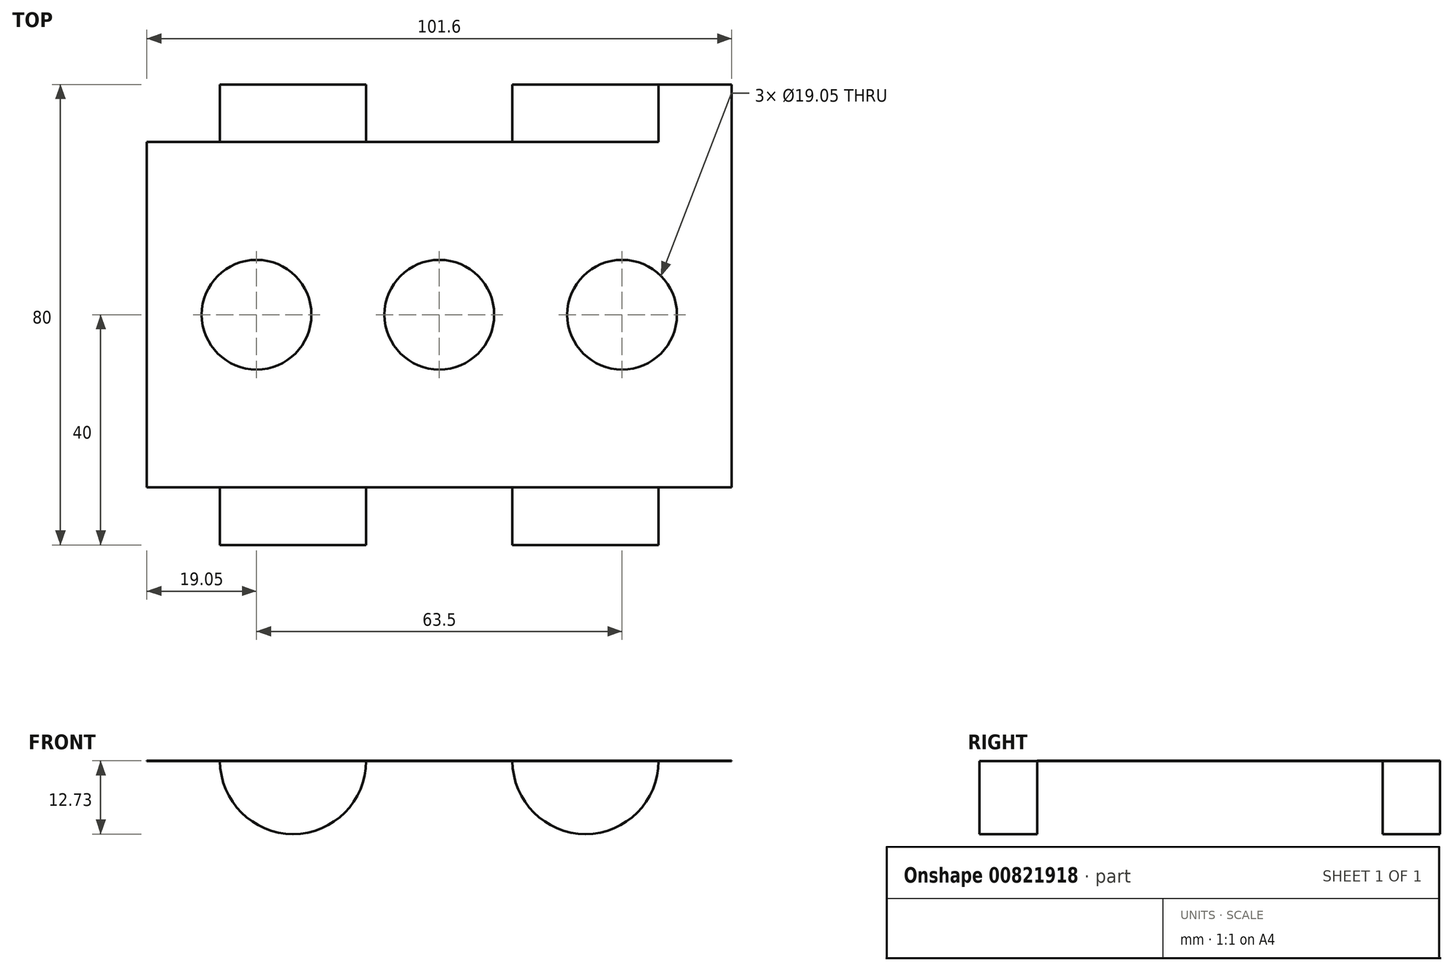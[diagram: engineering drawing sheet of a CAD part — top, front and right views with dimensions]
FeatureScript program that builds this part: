
annotation { "Feature Type Name" : "Feature", "Feature Type Description" : "" }
export const myFeature = defineFeature(function(context is Context, id is Id, definition is map)
    precondition{}
    {
        {
            var Q0;
            Q0=qCreatedBy(makeId("Top.planeOp"),FACE);
            var sketch = newSketch(context, id + "F0", { "sketchPlane" : qUnion([Q0])});
            skLineSegment(sketch, "E0.bottom", {"start": v(50.8, -30) * mm, "end": v(-50.8, -30) * mm});
            skLineSegment(sketch, "E0.top", {"start": v(50.8, 30) * mm, "end": v(-50.8, 30) * mm});
            skLineSegment(sketch, "E0.left", {"start": v(50.8, -30) * mm, "end": v(50.8, 30) * mm});
            skLineSegment(sketch, "E0.right", {"start": v(-50.8, -30) * mm, "end": v(-50.8, 30) * mm});
            skPoint(sketch, "E0.middle", {"position": v(0, 0) * mm});
            skSolve(sketch);
        }
        {
            var Q0;
            Q0=makeQuery(id+"F0.imprint","IMPRINT",FACE,{"disambiguationData":[TD([[makeQuery(id+"F0.imprint","IMPRINT",EDGE,{"derivedFrom":sQuery(id+"F0.wireOp",EDGE,"E0.bottom")}),-1.0]])]});
            extrude(context, id + "F1", {"entities" : qUnion([Q0]), "depth" : 3 / 101.6 * mm, "offsetDistance" : 25.4 * mm});
        }
        {
            var Q0;
            Q0=makeQuery(id+"F1.opExtrude","CAP_FACE",FACE,{"disambiguationData":[OSD([sQuery(id+"F0.wireOp",EDGE,"E0.bottom"),sQuery(id+"F0.wireOp",EDGE,"E0.top"),sQuery(id+"F0.wireOp",EDGE,"E0.left"),sQuery(id+"F0.wireOp",EDGE,"E0.right")])],"isStart":false});
            var sketch = newSketch(context, id + "F2", { "sketchPlane" : qUnion([Q0])});
            skLineSegment(sketch, "E1", {"start": v(0, 30) * mm, "end": v(0, -30) * mm, "construction": true});
            skLineSegment(sketch, "E2", {"start": v(-50.8, 0) * mm, "end": v(-31.75, 0) * mm, "construction": true});
            skLineSegment(sketch, "E3", {"start": v(31.75, 0) * mm, "end": v(50.8, 0) * mm, "construction": true});
            skCircle(sketch, "E4", {"center": v(-31.75, 0) * mm, "radius": 9.53 * mm});
            skCircle(sketch, "E5", {"center": v(0, 0) * mm, "radius": 9.53 * mm});
            skCircle(sketch, "E6", {"center": v(31.75, 0) * mm, "radius": 9.53 * mm});
            skLineSegment(sketch, "E7", {"start": v(-31.75, 0) * mm, "end": v(31.75, 0) * mm, "construction": true});
            skSolve(sketch);
        }
        {
            var Q0;
            Q0=makeQuery(id+"F2.imprint","IMPRINT",FACE,{"disambiguationData":[TD([[makeQuery(id+"F2.imprint","IMPRINT",EDGE,{"derivedFrom":sQuery(id+"F2.wireOp",EDGE,"E5")}),1.0]])]});
            var Q1;
            Q1=makeQuery(id+"F2.imprint","IMPRINT",FACE,{"disambiguationData":[TD([[makeQuery(id+"F2.imprint","IMPRINT",EDGE,{"derivedFrom":sQuery(id+"F2.wireOp",EDGE,"E6")}),1.0]])]});
            var Q2;
            Q2=makeQuery(id+"F2.imprint","IMPRINT",FACE,{"disambiguationData":[TD([[makeQuery(id+"F2.imprint","IMPRINT",EDGE,{"derivedFrom":sQuery(id+"F2.wireOp",EDGE,"E4")}),1.0]])]});
            extrude(context, id + "F3", {"entities" : qUnion([Q0, Q1, Q2]), "operationType" : NewBodyOperationType.REMOVE, "oppositeDirection" : true, "depth" : 6.35 * mm, "offsetDistance" : 25.4 * mm});
        }
        {
            var Q0;
            Q0=makeQuery(id+"F1.opExtrude","SWEPT_FACE",FACE,{"disambiguationData":[OSD([sQuery(id+"F0.wireOp",EDGE,"E0.top")])]});
            var sketch = newSketch(context, id + "F4", { "sketchPlane" : qUnion([Q0])});
            skLineSegment(sketch, "E8", {"start": v(-50.8, 0) * mm, "end": v(-25.4, 0) * mm});
            skLineSegment(sketch, "E9", {"start": v(-25.4, 0) * mm, "end": v(12.7, 0) * mm});
            skLineSegment(sketch, "E10", {"start": v(0, 0) * mm, "end": v(0, 19.05) * mm});
            skCircle(sketch, "E11", {"center": v(-25.4, 0) * mm, "radius": 12.7 * mm});
            skSolve(sketch);
        }
        {
            var Q0;
            {var subQ0=sQuery(id+"F4.wireOp",EDGE,"E8");Q0=makeQuery(id+"F4.imprint","IMPRINT",FACE,{"disambiguationData":[TD([[makeQuery(id+"F4.imprint","IMPRINT",EDGE,{"derivedFrom":subQ0}),1.0]])]});}
            var Q1;
            {var subQ0=sQuery(id+"F4.wireOp",EDGE,"E8");Q1=makeQuery(id+"F4.imprint","IMPRINT",FACE,{"disambiguationData":[TD([[makeQuery(id+"F4.imprint","IMPRINT",EDGE,{"derivedFrom":subQ0}),-1.0]])]});}
            extrude(context, id + "F5", {"entities" : qUnion([Q0, Q1]), "depth" : 10 * mm, "offsetDistance" : 25.4 * mm});
        }
        {
            var Q0;
            Q0=makeQuery(id+"F5.opExtrude","SWEPT_BODY",BODY,{"disambiguationData":[OSD([sQuery(id+"F4.wireOp",EDGE,"Uo6E3WlA-3b3M-Pep7-MsYb-nxxw53exLeKU")])]});
            var Q1;
            Q1=makeQuery(id+"F5.opExtrude","SWEPT_BODY",BODY,{"disambiguationData":[OSD([sQuery(id+"F4.wireOp",EDGE,"E11")])]});
            var Q2;
            Q2=qCreatedBy(makeId("Right.planeOp"),FACE);
            mirror(context, id + "F6", {"entities" : qUnion([Q0, Q1]), "mirrorPlane" : qUnion([Q2])});
        }
        {
            var Q0;
            Q0=makeQuery(id+"F6.opPattern","COPY",BODY,{"derivedFrom":makeQuery(id+"F5.opExtrude","SWEPT_BODY",BODY,{"disambiguationData":[OSD([sQuery(id+"F4.wireOp",EDGE,"Uo6E3WlA-3b3M-Pep7-MsYb-nxxw53exLeKU")])]}),"instanceName":"1"});
            var Q1;
            Q1=makeQuery(id+"F5.opExtrude","SWEPT_BODY",BODY,{"disambiguationData":[OSD([sQuery(id+"F4.wireOp",EDGE,"Uo6E3WlA-3b3M-Pep7-MsYb-nxxw53exLeKU")])]});
            var Q2;
            Q2=makeQuery(id+"F5.opExtrude","SWEPT_BODY",BODY,{"disambiguationData":[OSD([sQuery(id+"F4.wireOp",EDGE,"E11")])]});
            var Q3;
            Q3=makeQuery(id+"F6.opPattern","COPY",BODY,{"derivedFrom":makeQuery(id+"F5.opExtrude","SWEPT_BODY",BODY,{"disambiguationData":[OSD([sQuery(id+"F4.wireOp",EDGE,"E11")])]}),"instanceName":"1"});
            var Q4;
            Q4=qCreatedBy(makeId("Front.planeOp"),FACE);
            mirror(context, id + "F7", {"operationType" : NewBodyOperationType.ADD, "entities" : qUnion([Q0, Q1, Q2, Q3]), "mirrorPlane" : qUnion([Q4])});
        }
    });
